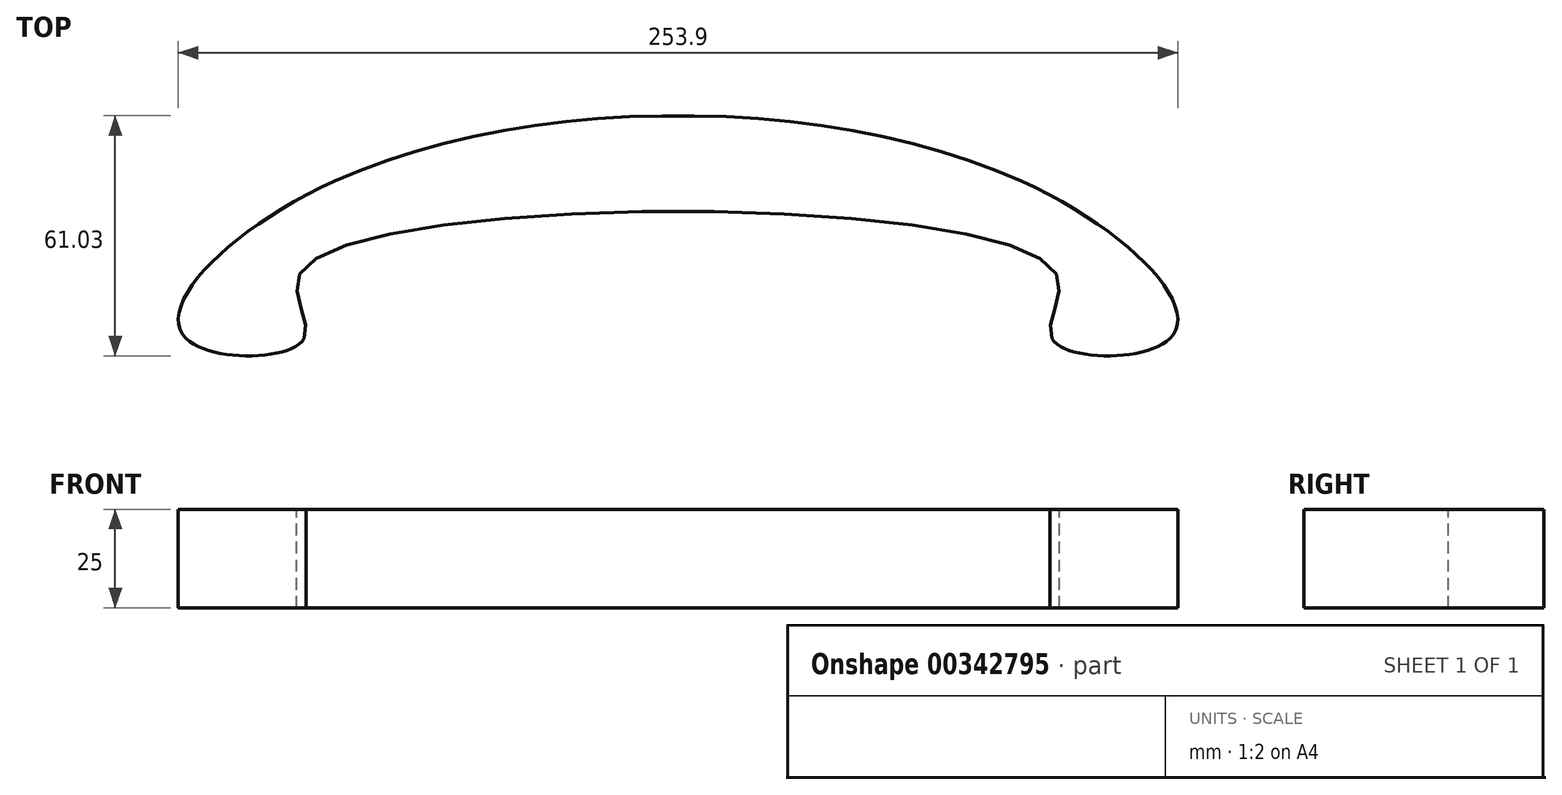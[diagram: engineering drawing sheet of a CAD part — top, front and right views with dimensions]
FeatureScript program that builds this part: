
annotation { "Feature Type Name" : "Feature", "Feature Type Description" : "" }
export const myFeature = defineFeature(function(context is Context, id is Id, definition is map)
    precondition{}
    {
        {
            var Q0;
            Q0=qCreatedBy(makeId("Top.planeOp"),FACE);
            var sketch = newSketch(context, id + "F0", { "sketchPlane" : qUnion([Q0])});
            skFitSpline(sketch, "E0", {"points": [v(-116.2, 0) * mm, v(-78.45, 40) * mm, v(96.05, 40) * mm, v(133.8, 0) * mm, v(103.8, 0) * mm, v(103.78, 18) * mm, v(-86.18, 18) * mm, v(-86.2, 0) * mm, v(-116.2, 0) * mm]});
            skLineSegment(sketch, "E1", {"start": v(-132.5, 0) * mm, "end": v(139.33, 0) * mm, "construction": true});
            skLineSegment(sketch, "E2", {"start": v(0, 40) * mm, "end": v(0, -63.5) * mm, "construction": true});
            skLineSegment(sketch, "E3", {"start": v(-116.2, 0) * mm, "end": v(-86.2, 0) * mm});
            skLineSegment(sketch, "E4", {"start": v(103.8, 0) * mm, "end": v(133.8, 0) * mm});
            skLineSegment(sketch, "E5", {"start": v(-78.45, 40) * mm, "end": v(96.05, 40) * mm});
            skSolve(sketch);
        }
        {
            var Q0;
            Q0=qSketchRegion(id+"F0",true);
            extrude(context, id + "F1", {"entities" : qUnion([Q0]), "depth" : 25 * mm});
        }
    });
